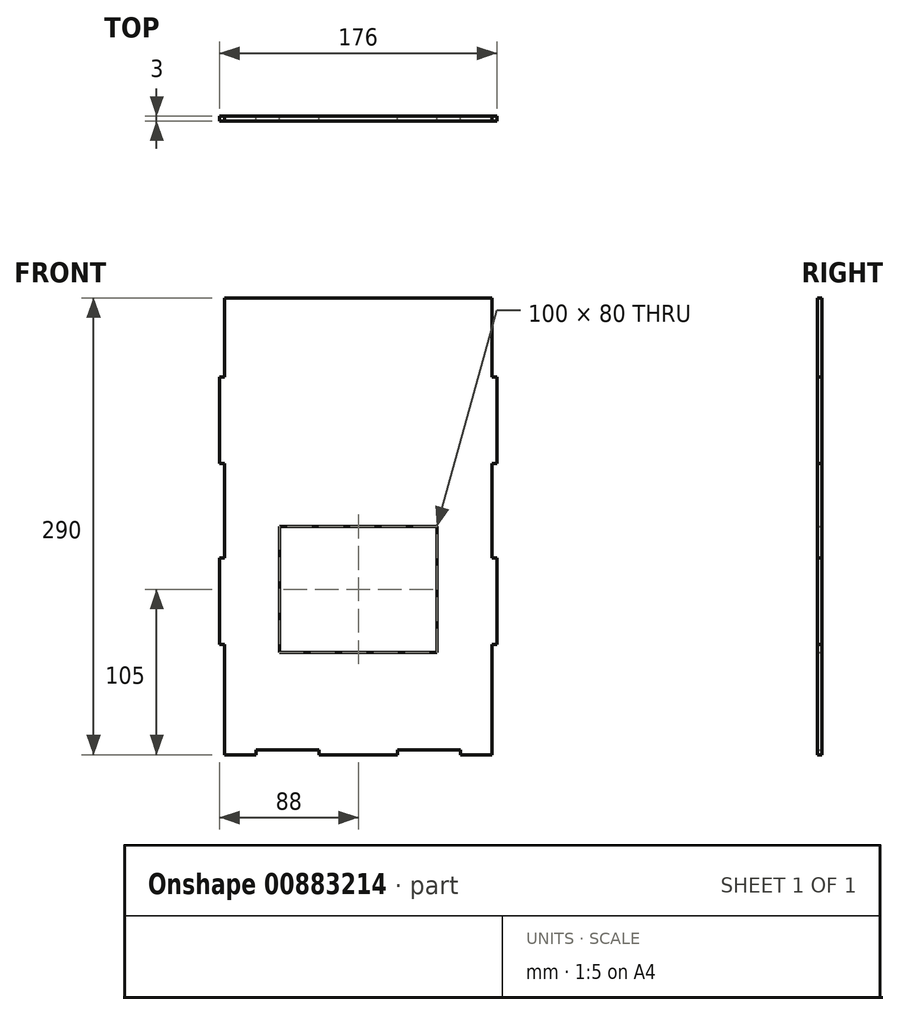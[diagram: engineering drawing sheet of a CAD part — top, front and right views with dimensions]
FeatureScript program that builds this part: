
annotation { "Feature Type Name" : "Feature", "Feature Type Description" : "" }
export const myFeature = defineFeature(function(context is Context, id is Id, definition is map)
    precondition{}
    {
        {
            var Q0;
            Q0=qCreatedBy(makeId("Front.planeOp"),FACE);
            var sketch = newSketch(context, id + "F0", { "sketchPlane" : qUnion([Q0])});
            skLineSegment(sketch, "E0.bottom", {"start": v(85, 145) * mm, "end": v(-85, 145) * mm});
            skLineSegment(sketch, "E0.top", {"start": v(85, -145) * mm, "end": v(-85, -145) * mm});
            skLineSegment(sketch, "E0.left", {"start": v(85, 145) * mm, "end": v(85, -145) * mm});
            skLineSegment(sketch, "E0.right", {"start": v(-85, 145) * mm, "end": v(-85, -145) * mm});
            skPoint(sketch, "E0.middle", {"position": v(0, 0) * mm});
            skLineSegment(sketch, "E1", {"start": v(25, -142) * mm, "end": v(65, -142) * mm});
            skLineSegment(sketch, "E2", {"start": v(65, -142) * mm, "end": v(65, -145) * mm});
            skLineSegment(sketch, "E3", {"start": v(25, -142) * mm, "end": v(25, -145) * mm});
            skLineSegment(sketch, "E4", {"start": v(85, -20) * mm, "end": v(88, -20) * mm});
            skLineSegment(sketch, "E5", {"start": v(88, -20) * mm, "end": v(88, -75) * mm});
            skLineSegment(sketch, "E6", {"start": v(88, -75) * mm, "end": v(85, -75) * mm});
            skLineSegment(sketch, "E7.MirrorCS", {"start": v(-85, -20) * mm, "end": v(-88, -20) * mm});
            skLineSegment(sketch, "E8.MirrorCS", {"start": v(-88, -20) * mm, "end": v(-88, -75) * mm});
            skLineSegment(sketch, "E9.MirrorCS", {"start": v(-88, -75) * mm, "end": v(-85, -75) * mm});
            skLineSegment(sketch, "E10", {"start": v(85, 95) * mm, "end": v(88, 95) * mm});
            skLineSegment(sketch, "E11", {"start": v(88, 95) * mm, "end": v(88, 40) * mm});
            skLineSegment(sketch, "E12", {"start": v(88, 40) * mm, "end": v(85, 40) * mm});
            skLineSegment(sketch, "E13.MirrorCS", {"start": v(-85, 95) * mm, "end": v(-88, 95) * mm});
            skLineSegment(sketch, "E14.MirrorCS", {"start": v(-88, 95) * mm, "end": v(-88, 40) * mm});
            skLineSegment(sketch, "E15.MirrorCS", {"start": v(-88, 40) * mm, "end": v(-85, 40) * mm});
            skLineSegment(sketch, "E16.MirrorCS", {"start": v(-25, -142) * mm, "end": v(-25, -145) * mm});
            skLineSegment(sketch, "E17.MirrorCS", {"start": v(-25, -142) * mm, "end": v(-65, -142) * mm});
            skLineSegment(sketch, "E18.MirrorCS", {"start": v(-65, -142) * mm, "end": v(-65, -145) * mm});
            skSolve(sketch);
        }
        {
            var Q0;
            Q0=makeQuery(id+"F0.imprint","IMPRINT",FACE,{"disambiguationData":[TD([[makeQuery(id+"F0.imprint","IMPRINT",EDGE,{"derivedFrom":sQuery(id+"F0.wireOp",EDGE,"E0.bottom")}),1.0]])]});
            var Q1;
            {var subQ0=sQuery(id+"F0.wireOp",EDGE,"E7.MirrorCS");Q1=makeQuery(id+"F0.imprint","IMPRINT",FACE,{"disambiguationData":[TD([[makeQuery(id+"F0.imprint","IMPRINT",EDGE,{"derivedFrom":subQ0}),1.0]])]});}
            var Q2;
            {var subQ0=sQuery(id+"F0.wireOp",EDGE,"E4");Q2=makeQuery(id+"F0.imprint","IMPRINT",FACE,{"disambiguationData":[TD([[makeQuery(id+"F0.imprint","IMPRINT",EDGE,{"derivedFrom":subQ0}),-1.0]])]});}
            var Q3;
            {var subQ0=sQuery(id+"F0.wireOp",EDGE,"E10");Q3=makeQuery(id+"F0.imprint","IMPRINT",FACE,{"disambiguationData":[TD([[makeQuery(id+"F0.imprint","IMPRINT",EDGE,{"derivedFrom":subQ0}),-1.0]])]});}
            var Q4;
            {var subQ0=sQuery(id+"F0.wireOp",EDGE,"E13.MirrorCS");Q4=makeQuery(id+"F0.imprint","IMPRINT",FACE,{"disambiguationData":[TD([[makeQuery(id+"F0.imprint","IMPRINT",EDGE,{"derivedFrom":subQ0}),1.0]])]});}
            extrude(context, id + "F1", {"entities" : qUnion([Q0, Q1, Q2, Q3, Q4]), "depth" : 3 * mm, "offsetDistance" : 25 * mm});
        }
        {
            var Q0;
            Q0=makeQuery(id+"F1.opExtrude","CAP_FACE",FACE,{"disambiguationData":[OSD([sQuery(id+"F0.wireOp",EDGE,"E0.bottom"),sQuery(id+"F0.wireOp",EDGE,"E0.top"),sQuery(id+"F0.wireOp",EDGE,"E0.left"),sQuery(id+"F0.wireOp",EDGE,"E0.right"),sQuery(id+"F0.wireOp",EDGE,"E1"),sQuery(id+"F0.wireOp",EDGE,"E2"),sQuery(id+"F0.wireOp",EDGE,"E3"),sQuery(id+"F0.wireOp",EDGE,"E4"),sQuery(id+"F0.wireOp",EDGE,"E5"),sQuery(id+"F0.wireOp",EDGE,"E6"),sQuery(id+"F0.wireOp",EDGE,"E7.MirrorCS"),sQuery(id+"F0.wireOp",EDGE,"E8.MirrorCS"),sQuery(id+"F0.wireOp",EDGE,"E9.MirrorCS")])],"isStart":true});
            var sketch = newSketch(context, id + "F2", { "sketchPlane" : qUnion([Q0])});
            skLineSegment(sketch, "E19.bottom", {"start": v(50, 0) * mm, "end": v(-50, 0) * mm});
            skLineSegment(sketch, "E19.top", {"start": v(50, -80) * mm, "end": v(-50, -80) * mm});
            skLineSegment(sketch, "E19.left", {"start": v(50, -80) * mm, "end": v(50, 0) * mm});
            skLineSegment(sketch, "E19.right", {"start": v(-50, -80) * mm, "end": v(-50, 0) * mm});
            skSolve(sketch);
        }
        {
            var Q0;
            Q0 = qSketchRegion(id + "F2", true);
            extrude(context, id + "F3", {"entities" : qUnion([Q0]), "operationType" : NewBodyOperationType.REMOVE, "endBound" : BoundingType.UP_TO_NEXT, "oppositeDirection" : true, "depth" : 25 * mm, "offsetDistance" : 25 * mm});
        }
    });
